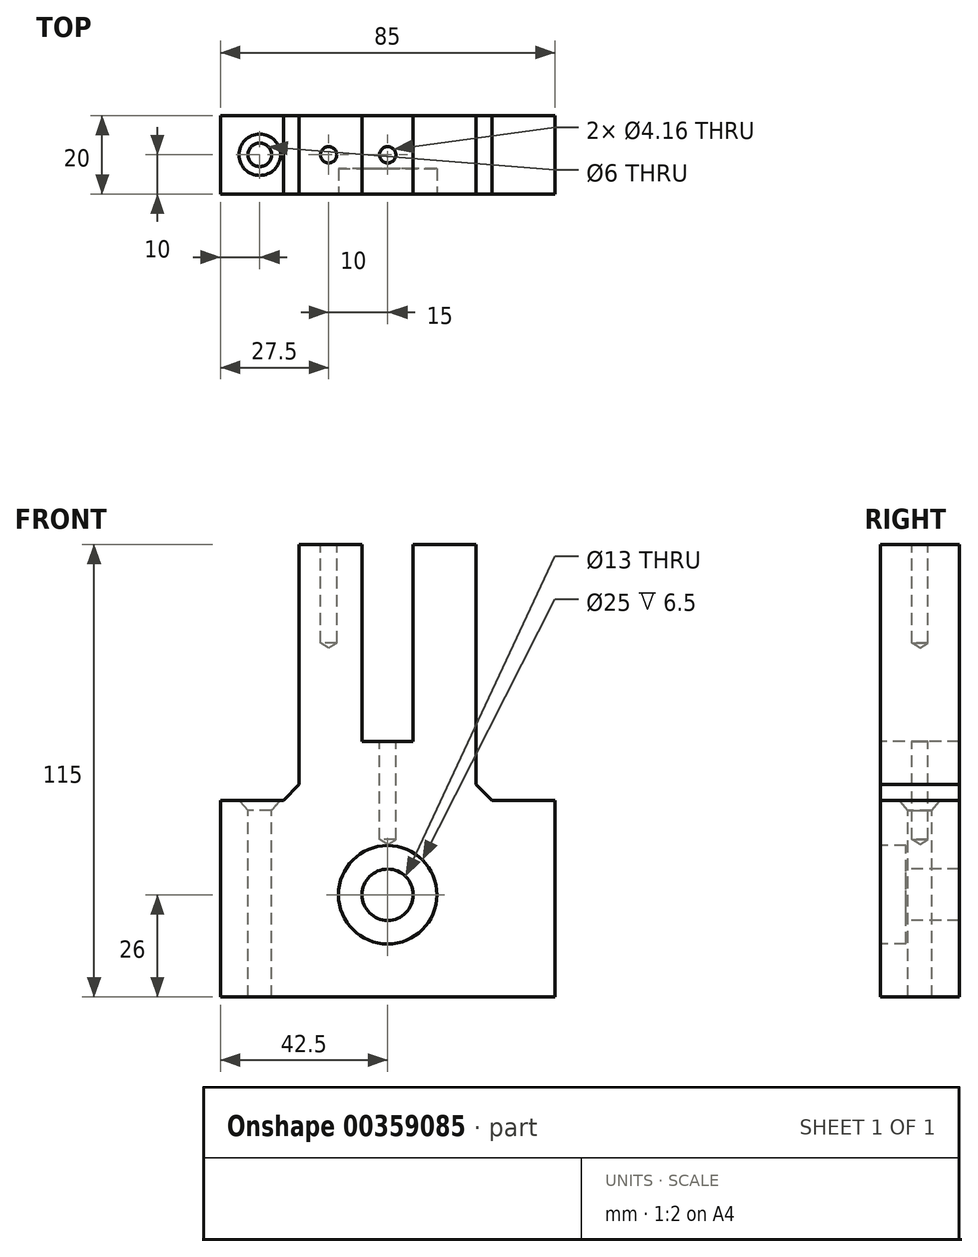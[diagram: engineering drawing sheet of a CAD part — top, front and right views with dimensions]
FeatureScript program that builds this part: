
annotation { "Feature Type Name" : "Feature", "Feature Type Description" : "" }
export const myFeature = defineFeature(function(context is Context, id is Id, definition is map)
    precondition{}
    {
        {
            var Q0;
            Q0=qCreatedBy(makeId("Front.planeOp"),FACE);
            var sketch = newSketch(context, id + "F0", { "sketchPlane" : qUnion([Q0])});
            skLineSegment(sketch, "E0.bottom", {"start": v(-42.5, 0) * mm, "end": v(42.5, 0) * mm});
            skLineSegment(sketch, "E0.top", {"start": v(-42.5, 50) * mm, "end": v(-22.5, 50) * mm});
            skLineSegment(sketch, "E0.left", {"start": v(-42.5, 0) * mm, "end": v(-42.5, 50) * mm});
            skLineSegment(sketch, "E0.right", {"start": v(42.5, 0) * mm, "end": v(42.5, 50) * mm});
            skLineSegment(sketch, "E1.top", {"start": v(-22.5, 115) * mm, "end": v(-6.5, 115) * mm});
            skLineSegment(sketch, "E1.left", {"start": v(-22.5, 50) * mm, "end": v(-22.5, 115) * mm});
            skLineSegment(sketch, "E1.right", {"start": v(22.5, 50) * mm, "end": v(22.5, 115) * mm});
            skLineSegment(sketch, "E2.trimOffspring", {"start": v(22.5, 50) * mm, "end": v(42.5, 50) * mm});
            skCircle(sketch, "E3", {"center": v(0, 26) * mm, "radius": 6.5 * mm});
            skLineSegment(sketch, "E4.top", {"start": v(-6.5, 65) * mm, "end": v(6.5, 65) * mm});
            skLineSegment(sketch, "E4.left", {"start": v(-6.5, 115) * mm, "end": v(-6.5, 65) * mm});
            skLineSegment(sketch, "E4.right", {"start": v(6.5, 115) * mm, "end": v(6.5, 65) * mm});
            skLineSegment(sketch, "E5.trimOffspring", {"start": v(6.5, 115) * mm, "end": v(22.5, 115) * mm});
            skSolve(sketch);
        }
        {
            var Q0;
            Q0=makeQuery(id+"F0.imprint","IMPRINT",FACE,{"disambiguationData":[TD([[makeQuery(id+"F0.imprint","IMPRINT",EDGE,{"derivedFrom":sQuery(id+"F0.wireOp",EDGE,"E0.bottom")}),1.0]])]});
            extrude(context, id + "F1", {"entities" : qUnion([Q0]), "endBound" : BoundingType.SYMMETRIC, "oppositeDirection" : true, "depth" : 20 * mm});
        }
        {
            var Q0;
            Q0=makeQuery(id+"F1.opExtrude","SWEPT_FACE",FACE,{"disambiguationData":[OSD([sQuery(id+"F0.wireOp",EDGE,"E0.top")])]});
            var sketch = newSketch(context, id + "F2", { "sketchPlane" : qUnion([Q0])});
            skPoint(sketch, "E6", {"position": v(-32.5, 0) * mm});
            skSolve(sketch);
        }
        {
            var Q0;
            Q0=sQuery(id+"F2.wireOp",VERTEX,"E6");
            var Q1;
            Q1=makeQuery(id+"F1.opExtrude","SWEPT_BODY",BODY,{"disambiguationData":[OSD([sQuery(id+"F0.wireOp",EDGE,"E0.bottom"),sQuery(id+"F0.wireOp",EDGE,"E0.top"),sQuery(id+"F0.wireOp",EDGE,"E0.left"),sQuery(id+"F0.wireOp",EDGE,"E0.right"),sQuery(id+"F0.wireOp",EDGE,"E1.top"),sQuery(id+"F0.wireOp",EDGE,"E1.left"),sQuery(id+"F0.wireOp",EDGE,"E1.right"),sQuery(id+"F0.wireOp",EDGE,"E2.trimOffspring"),sQuery(id+"F0.wireOp",EDGE,"E3"),sQuery(id+"F0.wireOp",EDGE,"E4.top"),sQuery(id+"F0.wireOp",EDGE,"E4.left"),sQuery(id+"F0.wireOp",EDGE,"E4.right"),sQuery(id+"F0.wireOp",EDGE,"E5.trimOffspring")])]});
            hole(context, id + "F3", {"style" : HoleStyle.C_SINK, "endStyle" : HoleEndStyle.THROUGH, "holeDiameter" : 6 * mm, "cSinkDiameter" : 10.5 * mm, "cSinkAngle" : 82 * degree, "isTappedThrough" : true, "tappedDepth" : 12 * mm, "tapClearance" : 3, "locations" : qUnion([Q0]), "scope" : qUnion([Q1])});
        }
        {
            var Q0;
            Q0=makeQuery(id+"F1.opExtrude","SWEPT_EDGE",EDGE,{"disambiguationData":[OSD([sQuery(id+"F0.wireOp",EDGE,"E0.top"),sQuery(id+"F0.wireOp",EDGE,"E1.left")])]});
            var Q1;
            Q1=makeQuery(id+"F1.opExtrude","SWEPT_EDGE",EDGE,{"disambiguationData":[OSD([sQuery(id+"F0.wireOp",EDGE,"E1.right"),sQuery(id+"F0.wireOp",EDGE,"E2.trimOffspring")])]});
            chamfer(context, id + "F4", {"entities" : qUnion([Q0, Q1]), "width" : 4 * mm, "tangentPropagation" : true});
        }
        {
            var Q0;
            Q0=makeQuery(id+"F1.opExtrude","SWEPT_FACE",FACE,{"disambiguationData":[OSD([sQuery(id+"F0.wireOp",EDGE,"E4.top")])]});
            var sketch = newSketch(context, id + "F5", { "sketchPlane" : qUnion([Q0])});
            skPoint(sketch, "E7", {"position": v(0, 0) * mm});
            skSolve(sketch);
        }
        {
            var Q0;
            Q0=sQuery(id+"F5.wireOp",VERTEX,"E7");
            var Q1;
            Q1=makeQuery(id+"F1.opExtrude","SWEPT_BODY",BODY,{"disambiguationData":[OSD([sQuery(id+"F0.wireOp",EDGE,"E0.bottom"),sQuery(id+"F0.wireOp",EDGE,"E0.top"),sQuery(id+"F0.wireOp",EDGE,"E0.left"),sQuery(id+"F0.wireOp",EDGE,"E0.right"),sQuery(id+"F0.wireOp",EDGE,"E1.top"),sQuery(id+"F0.wireOp",EDGE,"E1.left"),sQuery(id+"F0.wireOp",EDGE,"E1.right"),sQuery(id+"F0.wireOp",EDGE,"E2.trimOffspring"),sQuery(id+"F0.wireOp",EDGE,"E3"),sQuery(id+"F0.wireOp",EDGE,"E4.top"),sQuery(id+"F0.wireOp",EDGE,"E4.left"),sQuery(id+"F0.wireOp",EDGE,"E4.right"),sQuery(id+"F0.wireOp",EDGE,"E5.trimOffspring")])]});
            hole(context, id + "F6", {"style" : HoleStyle.SIMPLE, "endStyle" : HoleEndStyle.BLIND, "holeDiameter" : 4.16 * mm, "holeDepth" : 25 * mm, "isTappedThrough" : true, "tappedDepth" : 12 * mm, "tapClearance" : 3, "locations" : qUnion([Q0]), "scope" : qUnion([Q1])});
        }
        {
            var Q0;
            Q0=makeQuery(id+"F1.opExtrude","SWEPT_FACE",FACE,{"disambiguationData":[OSD([sQuery(id+"F0.wireOp",EDGE,"E1.top")])]});
            var sketch = newSketch(context, id + "F7", { "sketchPlane" : qUnion([Q0])});
            skPoint(sketch, "E8", {"position": v(-15, 0) * mm});
            skSolve(sketch);
        }
        {
            var Q0;
            Q0=sQuery(id+"F7.wireOp",VERTEX,"E8");
            var Q1;
            Q1=makeQuery(id+"F1.opExtrude","SWEPT_BODY",BODY,{"disambiguationData":[OSD([sQuery(id+"F0.wireOp",EDGE,"E0.bottom"),sQuery(id+"F0.wireOp",EDGE,"E0.top"),sQuery(id+"F0.wireOp",EDGE,"E0.left"),sQuery(id+"F0.wireOp",EDGE,"E0.right"),sQuery(id+"F0.wireOp",EDGE,"E1.top"),sQuery(id+"F0.wireOp",EDGE,"E1.left"),sQuery(id+"F0.wireOp",EDGE,"E1.right"),sQuery(id+"F0.wireOp",EDGE,"E2.trimOffspring"),sQuery(id+"F0.wireOp",EDGE,"E3"),sQuery(id+"F0.wireOp",EDGE,"E4.top"),sQuery(id+"F0.wireOp",EDGE,"E4.left"),sQuery(id+"F0.wireOp",EDGE,"E4.right"),sQuery(id+"F0.wireOp",EDGE,"E5.trimOffspring")])]});
            hole(context, id + "F8", {"style" : HoleStyle.SIMPLE, "endStyle" : HoleEndStyle.BLIND, "holeDiameter" : 4.16 * mm, "holeDepth" : 25 * mm, "isTappedThrough" : true, "tappedDepth" : 12 * mm, "tapClearance" : 3, "locations" : qUnion([Q0]), "scope" : qUnion([Q1])});
        }
        {
            var Q0;
            Q0=makeQuery(id+"F1.opExtrude","CAP_FACE",FACE,{"disambiguationData":[OSD([sQuery(id+"F0.wireOp",EDGE,"E0.bottom"),sQuery(id+"F0.wireOp",EDGE,"E0.top"),sQuery(id+"F0.wireOp",EDGE,"E0.left"),sQuery(id+"F0.wireOp",EDGE,"E0.right"),sQuery(id+"F0.wireOp",EDGE,"E1.top"),sQuery(id+"F0.wireOp",EDGE,"E1.left"),sQuery(id+"F0.wireOp",EDGE,"E1.right"),sQuery(id+"F0.wireOp",EDGE,"E2.trimOffspring"),sQuery(id+"F0.wireOp",EDGE,"E3"),sQuery(id+"F0.wireOp",EDGE,"E4.top"),sQuery(id+"F0.wireOp",EDGE,"E4.left"),sQuery(id+"F0.wireOp",EDGE,"E4.right"),sQuery(id+"F0.wireOp",EDGE,"E5.trimOffspring")])],"isStart":true});
            var sketch = newSketch(context, id + "F9", { "sketchPlane" : qUnion([Q0])});
            skPoint(sketch, "E9", {"position": v(0, 26) * mm});
            skCircle(sketch, "E10", {"center": v(0, 26) * mm, "radius": 12.5 * mm});
            skSolve(sketch);
        }
        {
            var Q0;
            Q0=makeQuery(id+"F9.imprint","IMPRINT",FACE,{"disambiguationData":[TD([[makeQuery(id+"F9.imprint","IMPRINT",EDGE,{"derivedFrom":sQuery(id+"F9.wireOp",EDGE,"E10")}),1.0]])]});
            extrude(context, id + "F10", {"entities" : qUnion([Q0]), "operationType" : NewBodyOperationType.REMOVE, "oppositeDirection" : true, "depth" : 6.5 * mm});
        }
    });
